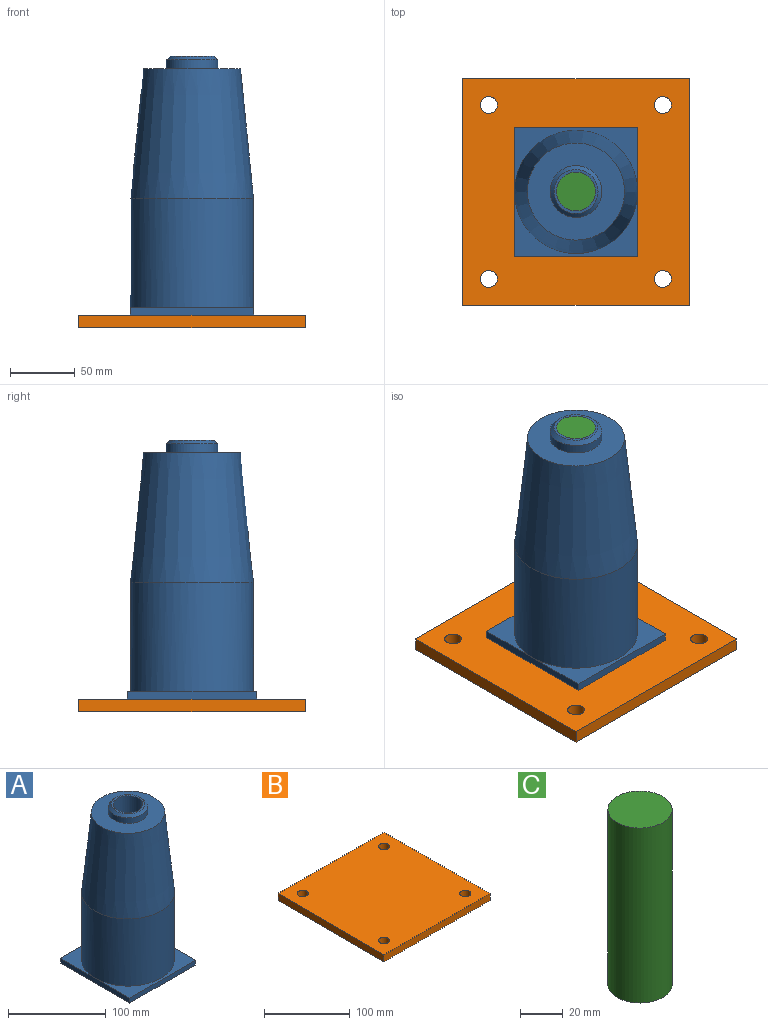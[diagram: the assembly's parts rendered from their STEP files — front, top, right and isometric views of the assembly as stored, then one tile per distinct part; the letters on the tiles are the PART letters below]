
ASSEMBLY  parts=3 mates=2
PART A: 15 faces, bbox 95x100x200 mm
  f0: cylinder r=47.5mm len=95mm, axis (0,0,-1), area 25069.9mm2, adj f6,f8,f9
  f1: plane 75x75mm, normal (0,0,1), area 3161.2mm2, adj f9,f10
  f2: plane 100x95mm, normal (0,0,-1), area 9500mm2, adj f3,f4,f5,f7
  f3: plane 95x6mm, normal (0,-1,0), area 570mm2, adj f2,f4,f5,f6
  f4: plane 100x6mm, normal (1,0,0), area 600mm2, adj f2,f3,f6,f7,f8
  f5: plane 100x6mm, normal (-1,0,0), area 600mm2, adj f2,f3,f6,f7,f8
  f6: plane 95x50mm, normal (0,0,1), area 1205.9mm2, adj f0,f3,f4,f5
  f7: plane 95x6mm, normal (0,1,0), area 570mm2, adj f2,f4,f5,f8
  f8: plane 95x50mm, normal (0,0,1), area 1205.9mm2, adj f0,f4,f5,f7
  f9: cone r=37.5mm half-angle=5.7deg, axis (0,0,-1), area 26836.7mm2, adj f0,f1
  f10: cylinder r=20mm len=40mm, axis (0,0,-1), area 879.6mm2, adj f1,f14
  f11: plane 34x34mm, normal (0,0,1), area 201.1mm2, adj f13,f14
  f12: plane 30x30mm, normal (0,0,1), area 706.9mm2, adj f13
  f13: cylinder r=15mm len=110mm, axis (0,0,1), area 10367.3mm2, adj f11,f12
  f14: cone r=17mm half-angle=45deg, axis (0,0,-1), area 493.2mm2, adj f10,f11
PART B: 10 faces, bbox 175x175x10 mm
  f0: plane 175x10mm, normal (0,-1,0), area 1750mm2, adj f1,f3,f4,f5
  f1: plane 175x10mm, normal (1,0,0), area 1750mm2, adj f0,f2,f4,f5
  f2: plane 175x10mm, normal (0,1,0), area 1750mm2, adj f1,f3,f4,f5
  f3: plane 175x10mm, normal (-1,0,0), area 1750mm2, adj f0,f2,f4,f5
  f4: plane 175x175mm, normal (0,0,-1), area 30094.1mm2, adj f0,f1,f2,f3,f6,f7,f8,f9
  f5: plane 175x175mm, normal (0,0,1), area 30094.1mm2, adj f0,f1,f2,f3,f6,f7,f8,f9
  f6: cylinder r=6.5mm len=13mm, axis (0,0,1), area 408.4mm2, adj f4,f5
  f7: cylinder r=6.5mm len=13mm, axis (0,0,1), area 408.4mm2, adj f4,f5
  f8: cylinder r=6.5mm len=13mm, axis (0,0,1), area 408.4mm2, adj f4,f5
  f9: cylinder r=6.5mm len=13mm, axis (0,0,1), area 408.4mm2, adj f4,f5
PART C: 3 faces, bbox 30x30x100 mm
  f0: cylinder r=15mm len=100mm, axis (0,0,-1), area 9424.8mm2, adj f1,f2
  f1: plane 30x30mm, normal (0,0,1), area 706.9mm2, adj f0
  f2: plane 30x30mm, normal (0,0,-1), area 706.9mm2, adj f0
PLACE A t=(174.71,-258.97,42.82)mm fixed
PLACE B t=(-599.84,-258.97,42.82)mm
PLACE C t=(199.03,-533.75,142.82)mm
MATE fastened B.f5 <-> A.f0  axis (0,0,1) through (-599.84,-258.97,42.82)mm
MATE slider C.f0 <-> A.f0  axis (0,0,1) through (-599.84,-258.97,242.82)mm
